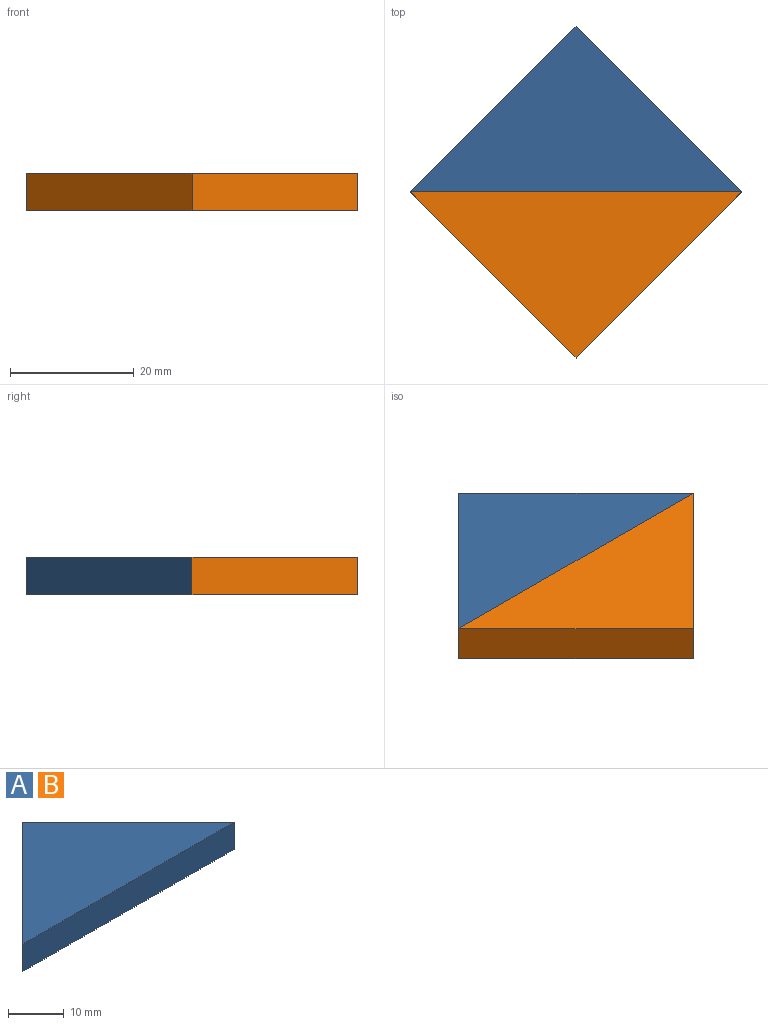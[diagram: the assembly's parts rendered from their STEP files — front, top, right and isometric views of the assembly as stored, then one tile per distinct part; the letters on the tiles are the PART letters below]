
ASSEMBLY  parts=2 mates=1
PART A: 5 faces, bbox 53.7x26.9x6 mm
  f0: plane 26.87x26.87mm, normal (-0.71,0.71,0), area 228mm2, adj f1,f2,f3,f4
  f1: plane 53.74x6mm, normal (0,-1,0), area 322.4mm2, adj f0,f2,f3,f4
  f2: plane 26.87x26.87mm, normal (0.71,0.71,0), area 228mm2, adj f0,f1,f3,f4
  f3: plane 53.74x26.87mm, normal (0,0,1), area 722mm2, adj f0,f1,f2
  f4: plane 53.74x26.87mm, normal (0,0,-1), area 722mm2, adj f0,f1,f2
PART B: same geometry as A
PLACE A t=(1.7,4.59,-0.7)mm
PLACE B rot(axis=(1,0,0),180deg) t=(1.7,4.59,5.3)mm
MATE fastened B.f1 <-> A.f1  axis (0,1,0) through (28.57,4.59,2.3)mm
